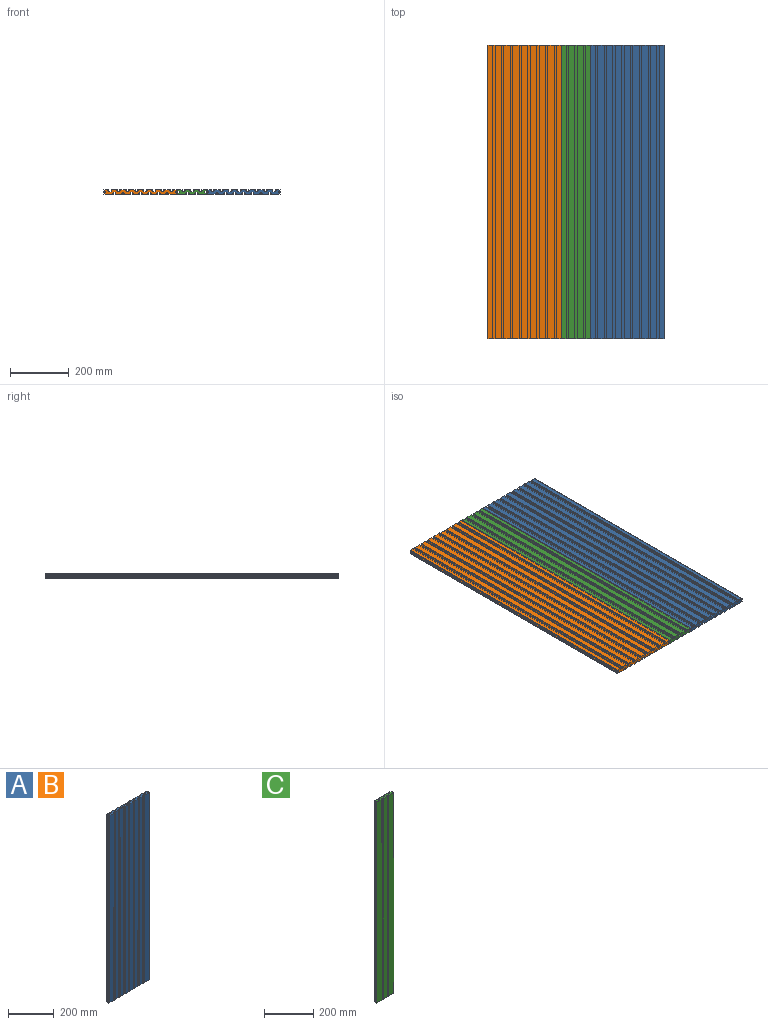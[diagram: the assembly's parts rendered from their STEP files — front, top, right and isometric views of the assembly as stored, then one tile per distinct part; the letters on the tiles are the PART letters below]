
ASSEMBLY  parts=3 mates=6
PART A: 142 faces, bbox 250x15x1000 mm
  f0: plane 1000x22mm, normal (0,1,0), area 22000mm2, adj f17,f18,f112,f135
  f1: plane 1000x22mm, normal (0,1,0), area 22000mm2, adj f17,f18,f128,f140
  f2: plane 1000x22mm, normal (0,1,0), area 22000mm2, adj f17,f18,f121,f133
  f3: plane 1000x22mm, normal (0,1,0), area 22000mm2, adj f17,f18,f105,f107
  f4: plane 1000x22mm, normal (0,1,0), area 22000mm2, adj f17,f18,f98,f100
  f5: plane 1000x22mm, normal (0,1,0), area 22000mm2, adj f17,f18,f91,f93
  f6: plane 1000x22mm, normal (0,1,0), area 22000mm2, adj f17,f18,f28,f86
  f7: plane 1000x16mm, normal (0,1,0), area 16000mm2, adj f8,f17,f18,f23
  f8: plane 1000x4.5mm, normal (-1,0,0), area 4500mm2, adj f7,f17,f18,f70
  f9: plane 1000x32mm, normal (0,-1,0), area 32000mm2, adj f17,f18,f20,f119
  f10: plane 1000x24mm, normal (0,-1,0), area 24000mm2, adj f17,f18,f51,f84
  f11: plane 1000x24mm, normal (0,-1,0), area 24000mm2, adj f17,f18,f77,f79
  f12: plane 1000x24mm, normal (0,-1,0), area 24000mm2, adj f17,f18,f44,f56
  f13: plane 1000x24mm, normal (0,-1,0), area 24000mm2, adj f17,f18,f37,f49
  f14: plane 1000x24mm, normal (0,-1,0), area 24000mm2, adj f17,f18,f30,f42
  f15: plane 1000x24mm, normal (0,-1,0), area 24000mm2, adj f17,f18,f35,f114
  f16: plane 1000x4.5mm, normal (1,0,0), area 4500mm2, adj f17,f18,f19,f58
  f17: plane 250x15mm, normal (0,0,1), area 2740mm2, adj f0,f1,f2,f3,f4,f5,f6,f7
  f18: plane 250x15mm, normal (0,0,-1), area 2740mm2, adj f0,f1,f2,f3,f4,f5,f6,f7
  f19: plane 1000x16mm, normal (0,1,0), area 16000mm2, adj f16,f17,f18,f126
  f20: plane 1000x4.5mm, normal (-1,0,0), area 4500mm2, adj f9,f17,f18,f65
  f21: plane 1000x32mm, normal (0,-1,0), area 32000mm2, adj f17,f18,f22,f72
  f22: plane 1000x4.5mm, normal (1,0,0), area 4500mm2, adj f17,f18,f21,f63
  f23: plane 1000x2mm, normal (1,0,0), area 2000mm2, adj f7,f17,f18,f24
  f24: plane 1000x3.25mm, normal (0,-1,0), area 3250mm2, adj f17,f18,f23,f25
  f25: plane 1000x5mm, normal (0.84,0.54,0), area 5963.4mm2, adj f17,f18,f24,f26
  f26: plane 1000x8mm, normal (0,1,0), area 8000mm2, adj f17,f18,f25,f27
  f27: plane 1000x5mm, normal (-0.84,0.54,0), area 5963.4mm2, adj f17,f18,f26,f29
  f28: plane 1000x2mm, normal (-1,0,0), area 2000mm2, adj f6,f17,f18,f29
  f29: plane 1000x3.25mm, normal (0,-1,0), area 3250mm2, adj f17,f18,f27,f28
  f30: plane 1000x2mm, normal (-1,0,0), area 2000mm2, adj f14,f17,f18,f31
  f31: plane 1000x3mm, normal (0,1,0), area 3000mm2, adj f17,f18,f30,f32
  f32: plane 1000x4mm, normal (-0.8,-0.6,0), area 5000mm2, adj f17,f18,f31,f33
  f33: plane 1000x6mm, normal (0,-1,0), area 6000mm2, adj f17,f18,f32,f34
  f34: plane 1000x4mm, normal (0.8,-0.6,0), area 5000mm2, adj f17,f18,f33,f36
  f35: plane 1000x2mm, normal (1,0,0), area 2000mm2, adj f15,f17,f18,f36
  f36: plane 1000x3mm, normal (0,1,0), area 3000mm2, adj f17,f18,f34,f35
  f37: plane 1000x2mm, normal (-1,0,0), area 2000mm2, adj f13,f17,f18,f38
  f38: plane 1000x3mm, normal (0,1,0), area 3000mm2, adj f17,f18,f37,f39
  f39: plane 1000x4mm, normal (-0.8,-0.6,0), area 5000mm2, adj f17,f18,f38,f40
  f40: plane 1000x6mm, normal (0,-1,0), area 6000mm2, adj f17,f18,f39,f41
  f41: plane 1000x4mm, normal (0.8,-0.6,0), area 5000mm2, adj f17,f18,f40,f43
  f42: plane 1000x2mm, normal (1,0,0), area 2000mm2, adj f14,f17,f18,f43
  f43: plane 1000x3mm, normal (0,1,0), area 3000mm2, adj f17,f18,f41,f42
  f44: plane 1000x2mm, normal (-1,0,0), area 2000mm2, adj f12,f17,f18,f45
  f45: plane 1000x3mm, normal (0,1,0), area 3000mm2, adj f17,f18,f44,f46
  f46: plane 1000x4mm, normal (-0.8,-0.6,0), area 5000mm2, adj f17,f18,f45,f47
  f47: plane 1000x6mm, normal (0,-1,0), area 6000mm2, adj f17,f18,f46,f48
  f48: plane 1000x4mm, normal (0.8,-0.6,0), area 5000mm2, adj f17,f18,f47,f50
  f49: plane 1000x2mm, normal (1,0,0), area 2000mm2, adj f13,f17,f18,f50
  f50: plane 1000x3mm, normal (0,1,0), area 3000mm2, adj f17,f18,f48,f49
  f51: plane 1000x2mm, normal (-1,0,0), area 2000mm2, adj f10,f17,f18,f52
  f52: plane 1000x3mm, normal (0,1,0), area 3000mm2, adj f17,f18,f51,f53
  f53: plane 1000x4mm, normal (-0.8,-0.6,0), area 5000mm2, adj f17,f18,f52,f54
  f54: plane 1000x6mm, normal (0,-1,0), area 6000mm2, adj f17,f18,f53,f55
  f55: plane 1000x4mm, normal (0.8,-0.6,0), area 5000mm2, adj f17,f18,f54,f57
  f56: plane 1000x2mm, normal (1,0,0), area 2000mm2, adj f12,f17,f18,f57
  f57: plane 1000x3mm, normal (0,1,0), area 3000mm2, adj f17,f18,f55,f56
  f58: plane 1000x2mm, normal (0,-1,0), area 2000mm2, adj f16,f17,f18,f59
  f59: plane 1000x3mm, normal (-1,0,0), area 3000mm2, adj f17,f18,f58,f60
  f60: plane 1000x4mm, normal (0.6,-0.8,0), area 5000mm2, adj f17,f18,f59,f61
  f61: plane 1000x6mm, normal (1,0,0), area 6000mm2, adj f17,f18,f60,f62
  f62: plane 1000x4mm, normal (0.6,0.8,0), area 5000mm2, adj f17,f18,f61,f64
  f63: plane 1000x2mm, normal (0,1,0), area 2000mm2, adj f17,f18,f22,f64
  f64: plane 1000x3mm, normal (-1,0,0), area 3000mm2, adj f17,f18,f62,f63
  f65: plane 1000x2mm, normal (0,1,0), area 2000mm2, adj f17,f18,f20,f66
  f66: plane 1000x3mm, normal (1,0,0), area 3000mm2, adj f17,f18,f65,f67
  f67: plane 1000x4mm, normal (-0.6,0.8,0), area 5000mm2, adj f17,f18,f66,f68
  f68: plane 1000x6mm, normal (-1,0,0), area 6000mm2, adj f17,f18,f67,f69
  f69: plane 1000x4mm, normal (-0.6,-0.8,0), area 5000mm2, adj f17,f18,f68,f71
  f70: plane 1000x2mm, normal (0,-1,0), area 2000mm2, adj f8,f17,f18,f71
  f71: plane 1000x3mm, normal (1,0,0), area 3000mm2, adj f17,f18,f69,f70
  f72: plane 1000x2mm, normal (-1,0,0), area 2000mm2, adj f17,f18,f21,f73
  f73: plane 1000x3mm, normal (0,1,0), area 3000mm2, adj f17,f18,f72,f74
  f74: plane 1000x4mm, normal (-0.8,-0.6,0), area 5000mm2, adj f17,f18,f73,f75
  f75: plane 1000x6mm, normal (0,-1,0), area 6000mm2, adj f17,f18,f74,f76
  f76: plane 1000x4mm, normal (0.8,-0.6,0), area 5000mm2, adj f17,f18,f75,f78
  f77: plane 1000x2mm, normal (1,0,0), area 2000mm2, adj f11,f17,f18,f78
  f78: plane 1000x3mm, normal (0,1,0), area 3000mm2, adj f17,f18,f76,f77
  f79: plane 1000x2mm, normal (-1,0,0), area 2000mm2, adj f11,f17,f18,f80
  f80: plane 1000x3mm, normal (0,1,0), area 3000mm2, adj f17,f18,f79,f81
  f81: plane 1000x4mm, normal (-0.8,-0.6,0), area 5000mm2, adj f17,f18,f80,f82
  f82: plane 1000x6mm, normal (0,-1,0), area 6000mm2, adj f17,f18,f81,f83
  f83: plane 1000x4mm, normal (0.8,-0.6,0), area 5000mm2, adj f17,f18,f82,f85
  f84: plane 1000x2mm, normal (1,0,0), area 2000mm2, adj f10,f17,f18,f85
  f85: plane 1000x3mm, normal (0,1,0), area 3000mm2, adj f17,f18,f83,f84
  f86: plane 1000x2mm, normal (1,0,0), area 2000mm2, adj f6,f17,f18,f87
  f87: plane 1000x3.25mm, normal (0,-1,0), area 3250mm2, adj f17,f18,f86,f88
  f88: plane 1000x5mm, normal (0.84,0.54,0), area 5963.4mm2, adj f17,f18,f87,f89
  f89: plane 1000x8mm, normal (0,1,0), area 8000mm2, adj f17,f18,f88,f90
  f90: plane 1000x5mm, normal (-0.84,0.54,0), area 5963.4mm2, adj f17,f18,f89,f92
  f91: plane 1000x2mm, normal (-1,0,0), area 2000mm2, adj f5,f17,f18,f92
  f92: plane 1000x3.25mm, normal (0,-1,0), area 3250mm2, adj f17,f18,f90,f91
  f93: plane 1000x2mm, normal (1,0,0), area 2000mm2, adj f5,f17,f18,f94
  f94: plane 1000x3.25mm, normal (0,-1,0), area 3250mm2, adj f17,f18,f93,f95
  f95: plane 1000x5mm, normal (0.84,0.54,0), area 5963.4mm2, adj f17,f18,f94,f96
  f96: plane 1000x8mm, normal (0,1,0), area 8000mm2, adj f17,f18,f95,f97
  f97: plane 1000x5mm, normal (-0.84,0.54,0), area 5963.4mm2, adj f17,f18,f96,f99
  f98: plane 1000x2mm, normal (-1,0,0), area 2000mm2, adj f4,f17,f18,f99
  f99: plane 1000x3.25mm, normal (0,-1,0), area 3250mm2, adj f17,f18,f97,f98
  f100: plane 1000x2mm, normal (1,0,0), area 2000mm2, adj f4,f17,f18,f101
  f101: plane 1000x3.25mm, normal (0,-1,0), area 3250mm2, adj f17,f18,f100,f102
  f102: plane 1000x5mm, normal (0.84,0.54,0), area 5963.4mm2, adj f17,f18,f101,f103
  f103: plane 1000x8mm, normal (0,1,0), area 8000mm2, adj f17,f18,f102,f104
  f104: plane 1000x5mm, normal (-0.84,0.54,0), area 5963.4mm2, adj f17,f18,f103,f106
  f105: plane 1000x2mm, normal (-1,0,0), area 2000mm2, adj f3,f17,f18,f106
  f106: plane 1000x3.25mm, normal (0,-1,0), area 3250mm2, adj f17,f18,f104,f105
  f107: plane 1000x2mm, normal (1,0,0), area 2000mm2, adj f3,f17,f18,f108
  f108: plane 1000x3.25mm, normal (0,-1,0), area 3250mm2, adj f17,f18,f107,f109
  f109: plane 1000x5mm, normal (0.84,0.54,0), area 5963.4mm2, adj f17,f18,f108,f110
  f110: plane 1000x8mm, normal (0,1,0), area 8000mm2, adj f17,f18,f109,f111
  f111: plane 1000x5mm, normal (-0.84,0.54,0), area 5963.4mm2, adj f17,f18,f110,f113
  f112: plane 1000x2mm, normal (-1,0,0), area 2000mm2, adj f0,f17,f18,f113
  f113: plane 1000x3.25mm, normal (0,-1,0), area 3250mm2, adj f17,f18,f111,f112
  f114: plane 1000x2mm, normal (-1,0,0), area 2000mm2, adj f15,f17,f18,f115
  f115: plane 1000x3mm, normal (0,1,0), area 3000mm2, adj f17,f18,f114,f116
  f116: plane 1000x4mm, normal (-0.8,-0.6,0), area 5000mm2, adj f17,f18,f115,f117
  f117: plane 1000x6mm, normal (0,-1,0), area 6000mm2, adj f17,f18,f116,f118
  f118: plane 1000x4mm, normal (0.8,-0.6,0), area 5000mm2, adj f17,f18,f117,f120
  f119: plane 1000x2mm, normal (1,0,0), area 2000mm2, adj f9,f17,f18,f120
  f120: plane 1000x3mm, normal (0,1,0), area 3000mm2, adj f17,f18,f118,f119
  f121: plane 1000x2mm, normal (1,0,0), area 2000mm2, adj f2,f17,f18,f122
  f122: plane 1000x3.25mm, normal (0,-1,0), area 3250mm2, adj f17,f18,f121,f123
  f123: plane 1000x5mm, normal (0.84,0.54,0), area 5963.4mm2, adj f17,f18,f122,f124
  f124: plane 1000x8mm, normal (0,1,0), area 8000mm2, adj f17,f18,f123,f125
  f125: plane 1000x5mm, normal (-0.84,0.54,0), area 5963.4mm2, adj f17,f18,f124,f127
  f126: plane 1000x2mm, normal (-1,0,0), area 2000mm2, adj f17,f18,f19,f127
  f127: plane 1000x3.25mm, normal (0,-1,0), area 3250mm2, adj f17,f18,f125,f126
  f128: plane 1000x2mm, normal (1,0,0), area 2000mm2, adj f1,f17,f18,f129
  f129: plane 1000x3.25mm, normal (0,-1,0), area 3250mm2, adj f17,f18,f128,f130
  f130: plane 1000x5mm, normal (0.84,0.54,0), area 5963.4mm2, adj f17,f18,f129,f131
  f131: plane 1000x8mm, normal (0,1,0), area 8000mm2, adj f17,f18,f130,f132
  f132: plane 1000x5mm, normal (-0.84,0.54,0), area 5963.4mm2, adj f17,f18,f131,f134
  f133: plane 1000x2mm, normal (-1,0,0), area 2000mm2, adj f2,f17,f18,f134
  f134: plane 1000x3.25mm, normal (0,-1,0), area 3250mm2, adj f17,f18,f132,f133
  f135: plane 1000x2mm, normal (1,0,0), area 2000mm2, adj f0,f17,f18,f136
  f136: plane 1000x3.25mm, normal (0,-1,0), area 3250mm2, adj f17,f18,f135,f137
  f137: plane 1000x5mm, normal (0.84,0.54,0), area 5963.4mm2, adj f17,f18,f136,f138
  f138: plane 1000x8mm, normal (0,1,0), area 8000mm2, adj f17,f18,f137,f139
  f139: plane 1000x5mm, normal (-0.84,0.54,0), area 5963.4mm2, adj f17,f18,f138,f141
  f140: plane 1000x2mm, normal (-1,0,0), area 2000mm2, adj f1,f17,f18,f141
  f141: plane 1000x3.25mm, normal (0,-1,0), area 3250mm2, adj f17,f18,f139,f140
PART B: same geometry as A
PART C: 62 faces, bbox 100x15x1000 mm
  f0: plane 1000x4.5mm, normal (-1,0,0), area 4500mm2, adj f1,f7,f8,f27
  f1: plane 1000x32mm, normal (0,-1,0), area 32000mm2, adj f0,f7,f8,f46
  f2: plane 1000x24mm, normal (0,-1,0), area 24000mm2, adj f7,f8,f39,f41
  f3: plane 1000x4.5mm, normal (1,0,0), area 4500mm2, adj f7,f8,f10,f25
  f4: plane 1000x22mm, normal (0,1,0), area 22000mm2, adj f7,f8,f18,f55
  f5: plane 1000x22mm, normal (0,1,0), area 22000mm2, adj f7,f8,f48,f60
  f6: plane 1000x16mm, normal (0,1,0), area 16000mm2, adj f7,f8,f9,f13
  f7: plane 100x15mm, normal (0,0,1), area 1091.3mm2, adj f0,f1,f2,f3,f4,f5,f6,f9
  f8: plane 100x15mm, normal (0,0,-1), area 1091.3mm2, adj f0,f1,f2,f3,f4,f5,f6,f9
  f9: plane 1000x4.5mm, normal (-1,0,0), area 4500mm2, adj f6,f7,f8,f32
  f10: plane 1000x32mm, normal (0,-1,0), area 32000mm2, adj f3,f7,f8,f34
  f11: plane 1000x4.5mm, normal (1,0,0), area 4500mm2, adj f7,f8,f12,f20
  f12: plane 1000x16mm, normal (0,1,0), area 16000mm2, adj f7,f8,f11,f53
  f13: plane 1000x2mm, normal (1,0,0), area 2000mm2, adj f6,f7,f8,f14
  f14: plane 1000x3.25mm, normal (0,-1,0), area 3250mm2, adj f7,f8,f13,f15
  f15: plane 1000x5mm, normal (0.84,0.54,0), area 5963.4mm2, adj f7,f8,f14,f16
  f16: plane 1000x8mm, normal (0,1,0), area 8000mm2, adj f7,f8,f15,f17
  f17: plane 1000x5mm, normal (-0.84,0.54,0), area 5963.4mm2, adj f7,f8,f16,f19
  f18: plane 1000x2mm, normal (-1,0,0), area 2000mm2, adj f4,f7,f8,f19
  f19: plane 1000x3.25mm, normal (0,-1,0), area 3250mm2, adj f7,f8,f17,f18
  f20: plane 1000x2mm, normal (0,-1,0), area 2000mm2, adj f7,f8,f11,f21
  f21: plane 1000x3mm, normal (-1,0,0), area 3000mm2, adj f7,f8,f20,f22
  f22: plane 1000x4mm, normal (0.6,-0.8,0), area 5000mm2, adj f7,f8,f21,f23
  f23: plane 1000x6mm, normal (1,0,0), area 6000mm2, adj f7,f8,f22,f24
  f24: plane 1000x4mm, normal (0.6,0.8,0), area 5000mm2, adj f7,f8,f23,f26
  f25: plane 1000x2mm, normal (0,1,0), area 2000mm2, adj f3,f7,f8,f26
  f26: plane 1000x3mm, normal (-1,0,0), area 3000mm2, adj f7,f8,f24,f25
  f27: plane 1000x2mm, normal (0,1,0), area 2000mm2, adj f0,f7,f8,f28
  f28: plane 1000x3mm, normal (1,0,0), area 3000mm2, adj f7,f8,f27,f29
  f29: plane 1000x4mm, normal (-0.6,0.8,0), area 5000mm2, adj f7,f8,f28,f30
  f30: plane 1000x6mm, normal (-1,0,0), area 6000mm2, adj f7,f8,f29,f31
  f31: plane 1000x4mm, normal (-0.6,-0.8,0), area 5000mm2, adj f7,f8,f30,f33
  f32: plane 1000x2mm, normal (0,-1,0), area 2000mm2, adj f7,f8,f9,f33
  f33: plane 1000x3mm, normal (1,0,0), area 3000mm2, adj f7,f8,f31,f32
  f34: plane 1000x2mm, normal (-1,0,0), area 2000mm2, adj f7,f8,f10,f35
  f35: plane 1000x3mm, normal (0,1,0), area 3000mm2, adj f7,f8,f34,f36
  f36: plane 1000x4mm, normal (-0.8,-0.6,0), area 5000mm2, adj f7,f8,f35,f37
  f37: plane 1000x6mm, normal (0,-1,0), area 6000mm2, adj f7,f8,f36,f38
  f38: plane 1000x4mm, normal (0.8,-0.6,0), area 5000mm2, adj f7,f8,f37,f40
  f39: plane 1000x2mm, normal (1,0,0), area 2000mm2, adj f2,f7,f8,f40
  f40: plane 1000x3mm, normal (0,1,0), area 3000mm2, adj f7,f8,f38,f39
  f41: plane 1000x2mm, normal (-1,0,0), area 2000mm2, adj f2,f7,f8,f42
  f42: plane 1000x3mm, normal (0,1,0), area 3000mm2, adj f7,f8,f41,f43
  f43: plane 1000x4mm, normal (-0.8,-0.6,0), area 5000mm2, adj f7,f8,f42,f44
  f44: plane 1000x6mm, normal (0,-1,0), area 6000mm2, adj f7,f8,f43,f45
  f45: plane 1000x4mm, normal (0.8,-0.6,0), area 5000mm2, adj f7,f8,f44,f47
  f46: plane 1000x2mm, normal (1,0,0), area 2000mm2, adj f1,f7,f8,f47
  f47: plane 1000x3mm, normal (0,1,0), area 3000mm2, adj f7,f8,f45,f46
  f48: plane 1000x2mm, normal (1,0,0), area 2000mm2, adj f5,f7,f8,f49
  f49: plane 1000x3.25mm, normal (0,-1,0), area 3250mm2, adj f7,f8,f48,f50
  f50: plane 1000x5mm, normal (0.84,0.54,0), area 5963.4mm2, adj f7,f8,f49,f51
  f51: plane 1000x8mm, normal (0,1,0), area 8000mm2, adj f7,f8,f50,f52
  f52: plane 1000x5mm, normal (-0.84,0.54,0), area 5963.4mm2, adj f7,f8,f51,f54
  f53: plane 1000x2mm, normal (-1,0,0), area 2000mm2, adj f7,f8,f12,f54
  f54: plane 1000x3.25mm, normal (0,-1,0), area 3250mm2, adj f7,f8,f52,f53
  f55: plane 1000x2mm, normal (1,0,0), area 2000mm2, adj f4,f7,f8,f56
  f56: plane 1000x3.25mm, normal (0,-1,0), area 3250mm2, adj f7,f8,f55,f57
  f57: plane 1000x5mm, normal (0.84,0.54,0), area 5963.4mm2, adj f7,f8,f56,f58
  f58: plane 1000x8mm, normal (0,1,0), area 8000mm2, adj f7,f8,f57,f59
  f59: plane 1000x5mm, normal (-0.84,0.54,0), area 5963.4mm2, adj f7,f8,f58,f61
  f60: plane 1000x2mm, normal (-1,0,0), area 2000mm2, adj f5,f7,f8,f61
  f61: plane 1000x3.25mm, normal (0,-1,0), area 3250mm2, adj f7,f8,f59,f60
PLACE A rot(axis=(1,0,0),90deg) t=(52.43,-800.51,73)mm
PLACE B rot(axis=(1,0,0),90deg) t=(-297.57,-800.51,73)mm
PLACE C rot(axis=(1,0,0),90deg) t=(-53.72,-800.51,128.65)mm
MATE planar B.f13 <-> A.f12  axis (0,0,-1) through (-565.82,-1300.51,-86.85)mm
MATE planar C.f7 <-> A.f17  axis (0,-1,0) through (-375.82,-1800.51,-79.74)mm
MATE planar C.f2 <-> B.f11  axis (0,0,-1) through (-375.82,-1300.51,-86.85)mm
MATE planar B.f22 <-> C.f0  axis (1,0,0) through (-425.82,-1300.51,-84.6)mm
MATE planar B.f17 <-> C.f7  axis (0,-1,0) through (-550.82,-1800.51,-79.64)mm
MATE planar A.f20 <-> C.f3  axis (-1,0,0) through (-325.82,-1300.51,-84.6)mm
